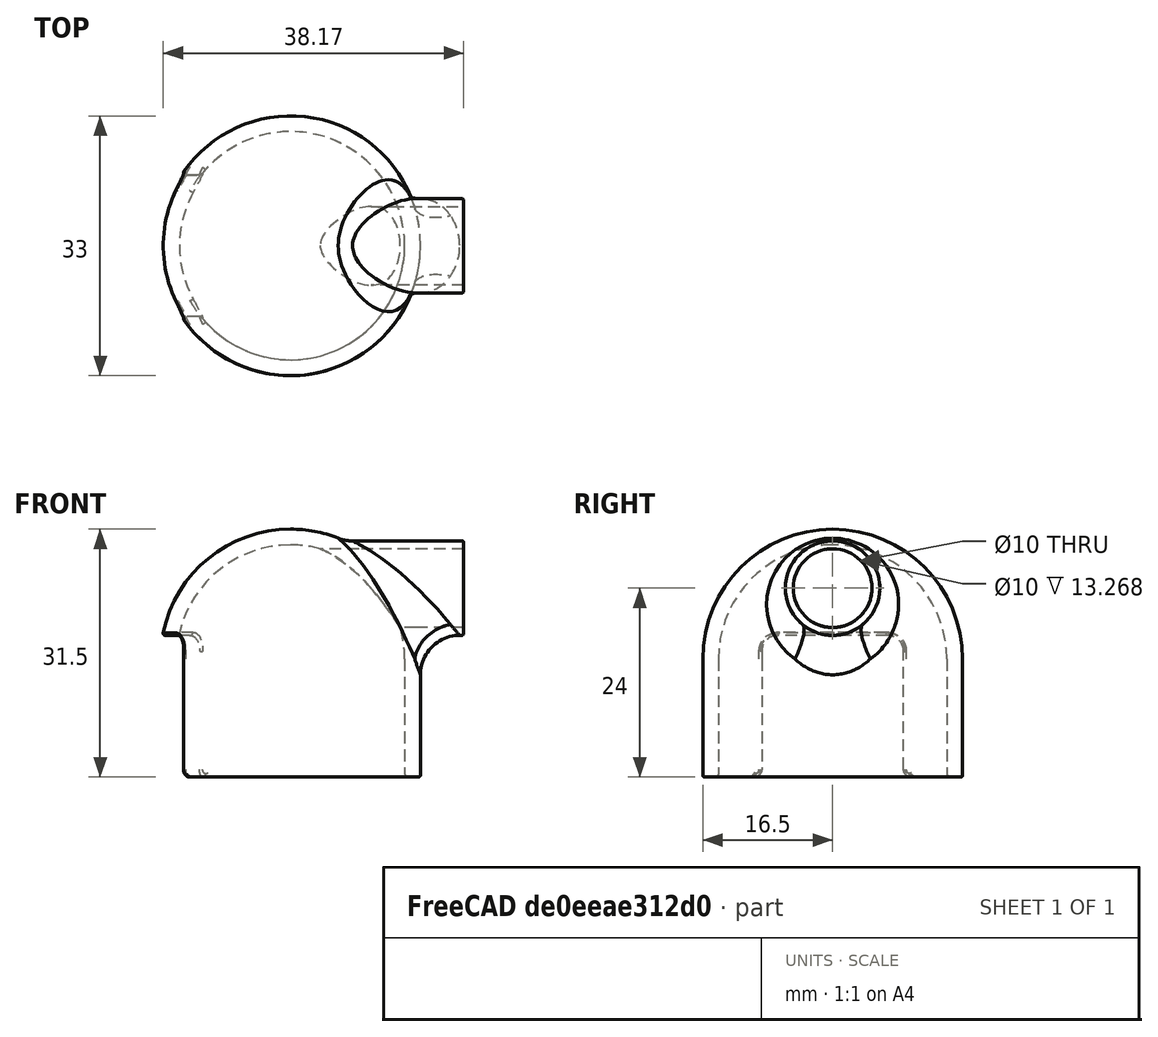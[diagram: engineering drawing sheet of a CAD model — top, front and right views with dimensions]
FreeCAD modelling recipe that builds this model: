
FCSTD DOCUMENT  (FreeCAD 0.16R)
Label: InstantPotDiverter
License: All rights reserved
LicenseURL: http://en.wikipedia.org/wiki/All_rights_reserved
objects: PartDesign::Fillet×6, Sketcher::SketchObject×3, PartDesign::Pad×2, PartDesign::Revolution×1, Part::Cut×1, Part::FeaturePython×1, Mesh::Feature×1
note: 17 computed .brp shape members not serialized (recipe doc carries the construction recipe); baked Part::Feature solids carry a one-line shape summary decoded from their .brp

FEATURE [Sketcher::SketchObject] Sketch
  Placement = pos=(0,0,0) rot=(1,0,0;1.5708rad)
  sketch-geometry (6):
    g0: LineSegment StartX=14.5 StartY=15 StartZ=0 EndX=14.5 EndY=0 EndZ=0
    g1: LineSegment StartX=14.5 StartY=0 StartZ=0 EndX=16.5 EndY=0 EndZ=0
    g2: LineSegment StartX=16.5 StartY=0 StartZ=0 EndX=16.5 EndY=15 EndZ=0
    g3: ArcOfCircle CenterX=0 CenterY=15 CenterZ=0 NormalX=0 NormalY=0 NormalZ=1 Radius=14.5 StartAngle=2.5852e-08 EndAngle=1.5708
    g4: ArcOfCircle CenterX=0 CenterY=15 CenterZ=0 NormalX=0 NormalY=0 NormalZ=1 Radius=16.5 StartAngle=6.28318 EndAngle=7.85398
    g5: LineSegment StartX=0 StartY=31.5 StartZ=0 EndX=0 EndY=29.5 EndZ=0
  constraints (20):
    c: Vertical(g0)
    c: Coincident(g0,g1)
    c: Horizontal(g1)
    c: Coincident(g1,g2)
    c: Vertical(g2)
    c: Coincident(g3,g0)
    c: PointOnObject(g3,g-2)
    c: Coincident(g4,g3)
    c: Coincident(g4,g2)
    c: DistanceX(g1,g1) = 2
    c: PointOnObject(g4,g-2)
    c: PointOnObject(g1,g-1)
    c: Vertical(g5)
    c: Coincident(g5,g4)
    c: Coincident(g5,g3)
    c: Tangent(g0,g3)
    c: Tangent(g2,g4)
    c: DistanceX(g0) = 14.5
    c: DistanceY(g2) = 15
    c: Perpendicular(g4,g-2)
FEATURE [PartDesign::Revolution] Revolution  label="Body"
  Angle = 360
  Axis = (0,0,1)
  Base = (0,0,0)
  Placement = pos=(0,0,0) rot=(1,0,0;1.5708rad)
  ReferenceAxis = -> Sketch [V_Axis]
  Reversed = true
  Sketch = -> Sketch
FEATURE [Sketcher::SketchObject] Sketch001
  Placement = pos=(0,0,0) rot=(0.57735,0.57735,0.57735;2.0944rad)
  sketch-geometry (2):
    g0: Circle CenterX=0 CenterY=24 CenterZ=0 NormalX=0 NormalY=0 NormalZ=1 Radius=6
    g1: Circle CenterX=0 CenterY=24 CenterZ=0 NormalX=0 NormalY=0 NormalZ=1 Radius=5
  constraints (5):
    c: Radius(g0) = 6
    c: DistanceY(g-1,g0) = 24
    c: Coincident(g1,g0)
    c: PointOnObject(g0,g-2)
    c: Radius(g1) = 5
FEATURE [PartDesign::Pad] Pad  label="Spout"
  Length = 22
  Length2 = 1
  Placement = pos=(0,0,0) rot=(0.57735,0.57735,0.57735;2.0944rad)
  Sketch = -> Sketch001
  Type = 0
FEATURE [Sketcher::SketchObject] Sketch002
  Placement = pos=(0,0,0) rot=(0.57735,0.57735,0.57735;2.0944rad)
  sketch-geometry (4):
    g0: LineSegment StartX=-9 StartY=18 StartZ=0 EndX=9 EndY=18 EndZ=0
    g1: LineSegment StartX=9 StartY=18 StartZ=0 EndX=9 EndY=-18 EndZ=0
    g2: LineSegment StartX=9 StartY=-18 StartZ=0 EndX=-9 EndY=-18 EndZ=0
    g3: LineSegment StartX=-9 StartY=-18 StartZ=0 EndX=-9 EndY=18 EndZ=0
  constraints (11):
    c: Coincident(g0,g1)
    c: Coincident(g1,g2)
    c: Coincident(g2,g3)
    c: Coincident(g3,g0)
    c: Horizontal(g0)
    c: Horizontal(g2)
    c: Vertical(g1)
    c: Vertical(g3)
    c: Symmetric(g1,g0,g-1)
    c: DistanceX(g0,g0) = 18
    c: DistanceY(g0) = 18
FEATURE [PartDesign::Pad] Pad001  label="Slot"
  Length = 20
  Length2 = 100
  Placement = pos=(0,0,0) rot=(0.57735,0.57735,0.57735;2.0944rad)
  Reversed = true
  Sketch = -> Sketch002
  Type = 0
FEATURE [Part::Cut] Cut
  Base = -> Revolution
  Tool = -> Pad001
FEATURE [Part::FeaturePython] Connect  # WARN: FeaturePython — macro-defined, semantics opaque (R4)
  Base = -> Cut
  Mode = 1
  Tool = -> Pad
FEATURE [PartDesign::Fillet] Fillet
  Base = -> Connect [Edge33]
  Radius = 5
FEATURE [PartDesign::Fillet] Fillet001
  Base = -> Fillet [Edge31,Edge21]
  Radius = 2
FEATURE [PartDesign::Fillet] Fillet002
  Base = -> Fillet001 [Edge32,Edge16]
  Radius = 1
FEATURE [PartDesign::Fillet] Fillet003
  Base = -> Fillet002 [Edge69]
  Radius = 0.25
FEATURE [PartDesign::Fillet] Fillet004
  Base = -> Fillet003 [Edge49]
  Radius = 0.5
FEATURE [PartDesign::Fillet] Fillet005
  Base = -> Fillet004 [Edge20]
  Radius = 0.25
FEATURE [Mesh::Feature] Mesh  label="Fillet005 (Meshed)"
